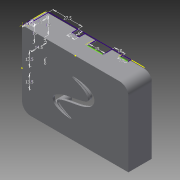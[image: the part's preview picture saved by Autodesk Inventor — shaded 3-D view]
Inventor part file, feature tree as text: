
AUTODESK INVENTOR PART (.ipt)
format: ipt  version: 2015 (Build 190159000, 159)  size: 377,344 bytes
history: native  units: mm
features: extrude x10, other x10, sketch x5, shell x1, chamfer x1
ambient origin geometry x8: Origin, YZ Plane, XZ Plane, XY Plane, X Axis, Y Axis, Z Axis, Center Point
bodies: Solid1 (feature_tree), Body (feature_tree)
feature tree (27):
  shell  "case"  Thickness=23.0mm
  extrude  "border"  Depth=70.0mm
  extrude  "logo"  Depth=35.0mm
  extrude  "frontHoles"  Depth=2.0mm
  extrude  "lateralHoles"  Depth=1.0mm
  other  "reinforcementPlane1"
  extrude  "reinforcement1"  Depth=2.0mm TaperAngle=0.0deg
  other  "reinforcementPlane2"
  extrude  "reinforcement2"  Depth=2.0mm TaperAngle=0.0deg
  other  "reinforcementPlane3"
  sketch  "Sketch15"  dims[d179=8.0mm d180=2.0mm]
  extrude  "reinforcement3"  Depth=10.0mm
  other  "reinforcementPlane4"
  extrude  "reinforcement4"  Depth=2.0mm
  extrude  "reinforcement4Hole"  Depth=2.0mm
  extrude  "screwHolders"  Depth=2.0mm
  chamfer  "Chamfer1"  Distance=16.0mm
  other  "baseBody"
  other  "LogoSketch"
  other  "baseBorder"
  other  "baseFrontHoles"
  other  "baseLateralHoles"
  sketch  "Sketch12"  dims[d175=100.0mm d176=70.0mm]
  sketch  "Sketch14"  dims[d177=50.0mm d178=35.0mm]
  sketch  "Sketch16"  dims[d181=8.0mm d182=1.0mm]
  sketch  "Sketch17"  dims[d183=1.0mm d184=1.0mm d185=0.0mm d186=11.0mm d187=0.0mm d188=10.0mm d189=4.5mm d190=16.0mm d191=13.0mm d192=16.0mm d193=4.0mm d194=14.5mm d195=13.5mm d196=5.0mm d197=13.5mm d198=10.0mm d199=0.0mm d201=27.5mm d202=6.0mm d203=7.0mm d204=15.0mm d205=10.0mm d206=7.5mm d207=11.0mm d208=0.0mm d209=-1.0mm d210=2.0mm d211=0.0mm d212=-1.0mm d213=3.0mm d214=0.0mm d215=-1.0mm d216=-1.0mm d219=8.0mm d220=0.0mm d221=8.5mm d222=0.0mm d223=3.0mm d224=5.0mm d225=3.0mm d226=5.0mm d227=10.0mm d228=0.0mm d229=23.575mm d230=48.95mm d231=57.5mm d232=2.5mm d233=2.5mm d234=2.5mm d235=2.5mm d236=6.0mm d237=6.0mm d238=6.0mm d239=6.0mm d240=16.5mm d241=0.0mm d242=4.350517mm d243=2.0mm d244=2.0mm d245=45.0deg]
  other  "baseScrewHoders"
